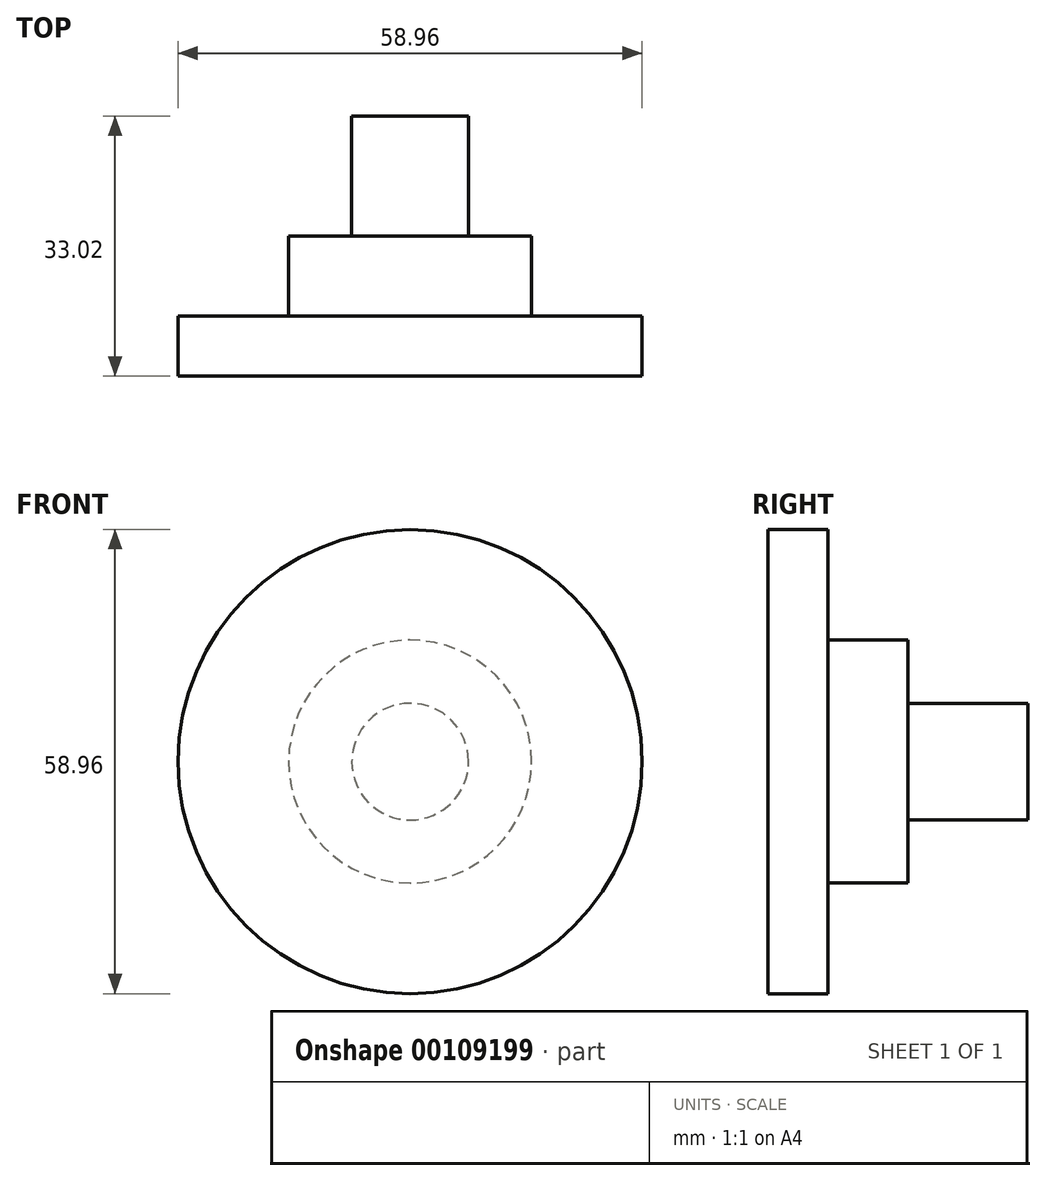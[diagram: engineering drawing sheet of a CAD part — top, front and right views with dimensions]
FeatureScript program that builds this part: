
annotation { "Feature Type Name" : "Feature", "Feature Type Description" : "" }
export const myFeature = defineFeature(function(context is Context, id is Id, definition is map)
    precondition{}
    {
        {
            var Q0;
            Q0=qCreatedBy(makeId("Front.planeOp"),FACE);
            var sketch = newSketch(context, id + "F0", { "sketchPlane" : qUnion([Q0])});
            skCircle(sketch, "E0", {"center": v(0, 0) * mm, "radius": 15.43 * mm});
            skCircle(sketch, "E1", {"center": v(0, 0) * mm, "radius": 29.48 * mm});
            skCircle(sketch, "E2", {"center": v(0, 0) * mm, "radius": 7.42 * mm});
            skSolve(sketch);
        }
        {
            var Q0;
            Q0=makeQuery(id+"F0.imprint","IMPRINT",FACE,{"disambiguationData":[TD([[makeQuery(id+"F0.imprint","IMPRINT",EDGE,{"derivedFrom":sQuery(id+"F0.wireOp",EDGE,"E2")}),1.0]])]});
            var Q1;
            Q1=makeQuery(id+"F0.imprint","IMPRINT",FACE,{"disambiguationData":[TD([[makeQuery(id+"F0.imprint","IMPRINT",EDGE,{"derivedFrom":sQuery(id+"F0.wireOp",EDGE,"E0")}),1.0]])]});
            var Q2;
            Q2=makeQuery(id+"F0.imprint","IMPRINT",FACE,{"disambiguationData":[TD([[makeQuery(id+"F0.imprint","IMPRINT",EDGE,{"derivedFrom":sQuery(id+"F0.wireOp",EDGE,"E0")}),-1.0]])]});
            extrude(context, id + "F1", {"entities" : qUnion([Q0, Q1, Q2]), "depth" : 7.62 * mm});
        }
        {
            var Q0;
            Q0=makeQuery(id+"F0.imprint","IMPRINT",FACE,{"disambiguationData":[TD([[makeQuery(id+"F0.imprint","IMPRINT",EDGE,{"derivedFrom":sQuery(id+"F0.wireOp",EDGE,"E0")}),1.0]])]});
            var Q1;
            Q1=makeQuery(id+"F0.imprint","IMPRINT",FACE,{"disambiguationData":[TD([[makeQuery(id+"F0.imprint","IMPRINT",EDGE,{"derivedFrom":sQuery(id+"F0.wireOp",EDGE,"E2")}),1.0]])]});
            extrude(context, id + "F2", {"entities" : qUnion([Q0, Q1]), "operationType" : NewBodyOperationType.ADD, "oppositeDirection" : true, "depth" : 10.16 * mm});
        }
        {
            var Q0;
            Q0=makeQuery(id+"F0.imprint","IMPRINT",FACE,{"disambiguationData":[TD([[makeQuery(id+"F0.imprint","IMPRINT",EDGE,{"derivedFrom":sQuery(id+"F0.wireOp",EDGE,"E2")}),1.0]])]});
            extrude(context, id + "F3", {"entities" : qUnion([Q0]), "operationType" : NewBodyOperationType.ADD, "oppositeDirection" : true, "depth" : 25.4 * mm});
        }
    });
